# Revit family: Hager-GOLF-Flush_mounted-IP40-With_Cover-With_DIN-Hosted-CH-de
name_source: partatom
category: Electrical Equipment
units: mm (PartAtom-declared; Revit-internal decimal feet)

## family parameters
Cut with Voids When Loaded = No
Host = Face
Maintain Annotation Orientation = Yes
Panel Configuration = Two Columns, Circuits Across
Part Type = Panelboard
Room Calculation Point = No
Round Connector Dimension = Use Diameter
Shared = No

## types (20) — shared parameters
BC_MODEL_ID = 1539115
BC_OBJECT_ID = 512264
BC_OBJECT_VERSION = #40
Code hager = ADD-EC000214_EU
EF000003 - Montageart = Unterputz
EF000007 - Farbe = weiss
EF000024 - UV-beständig = No
EF000049 - Tiefe = 97 mm  [stored 0.318241 ft]
EF000116 - RAL-Nummer = 9010
EF000118 - Mit Montageplatte = No
EF000218 - Einbautiefe = 72 mm  [stored 0.23622 ft]
EF001062 - EMV-Ausführung = No
EF001088 - Anbaumöglichkeit = Yes
EF001134 - DIN-Schiene = Yes
EF004462 - Art der Schliessung = sonstige
EF005474 - Schutzart (IP) = IP40
EF006306 - Mit Schloss = No
EF009212 - Ausführung Deckel = geschlossen
EF015941 - Signaldurchlassende Tür = Yes
ETIM class code = EC000214
ETIM class name = Small distribution board
HG000001-Anzahl der Spalten = 1
HG000002-Mit tür = Yes
HG000003-Bereich = GOLF
HG000005-Dicke = 2 mm  [stored 0.00656168 ft]
HG000006-Unterputz = Yes
HG000009-Doppelflügeligen Tür = No
HG000010-Asymmetrische Türen = No
HG000011-Leere Reihen von unten = No
HG000012-Türschwenkwinkel = 90.00°
HG000013-Tür links = No
HG000014-Tür rechts = Yes
HG000015-Sichtbarkeit der Türöffnung = Yes
HG000016-3D-Türsichtbarkeit = Yes
HG000017-Distanz zwischen den Polen = 18 mm  [stored 0.0590551 ft]
HG000060-RAL-number = 9010
HG000099-Onfly Template ID-de-CH = 507532
Manufacturer = Hager
Name = Hager-GOLF-Flush_mounted-IP40-With_Cover-With_DIN-NoHosted-CH-de
Name BIM&CO = Electricity
Name hager = ADD_Enclosures_EC000214
Uniformat = Low Tension Service & Dist.
Uniformat code = D501001
zero-valued in all types: Default Elevation, EF001131 - Innentiefe, HG000007-Anzahl der leeren Spalten, HG000008-Anzahl der leeren Reihen

## per-type parameters (varying)
| type | BC_VARIANT_ID | EF000008 - Breite | EF000040 - Höhe | EF000266 - Anzahl der Reihen | EF000332 - Einbauhöhe | EF000846 - Einbaubreite | EF002950 - Anzahl Teilungseinheiten | EF006244 - Transparenter Deckel/Tür | EF015776 - Erdungsklemmenblock | EF015777 - Neutralleiterklemmenblock | HG000004-Herstellerreferenz | HGEF000266-Anzahl der Reihen | HGEF0002950-Breite in Teilungseinheiten |
| GOLF-Flush_mounted_W204_H225_D97_4_Modular_Spacing-VF104PS | 1169077 | 204 mm | 225 mm  [stored 0.738189 ft] | 1 | 189 mm  [stored 0.620079 ft] | 170 mm  [stored 0.557743 ft] | 4 | No | No | No | VF104PS | 1 | 4 |
| GOLF-Flush_mounted_W204_H225_D97_4_Modular_Spacing-VF104TS | 1169078 | 204 mm | 225 mm  [stored 0.738189 ft] | 1 | 189 mm  [stored 0.620079 ft] | 170 mm  [stored 0.557743 ft] | 4 | Yes | No | No | VF104TS | 1 | 4 |
| GOLF-Flush_mounted_W275_H225_D97_8_Modular_Spacing-VF108PS | 1169079 | 275 mm | 225 mm  [stored 0.738189 ft] | 1 | 189 mm  [stored 0.620079 ft] | 242 mm  [stored 0.793963 ft] | 8 | No | No | No | VF108PS | 1 | 8 |
| GOLF-Flush_mounted_W275_H225_D97_8_Modular_Spacing-VF108TS | 1169080 | 275 mm | 225 mm  [stored 0.738189 ft] | 1 | 189 mm  [stored 0.620079 ft] | 242 mm  [stored 0.793963 ft] | 8 | Yes | No | No | VF108TS | 1 | 8 |
| GOLF-Flush_mounted_W352_H293_D97_12_Modular_Spacing-VF112PS | 1169081 | 352 mm  [stored 1.15486 ft] | 293 mm | 1 | 257 mm  [stored 0.843176 ft] | 318 mm  [stored 1.04331 ft] | 12 | No | Yes | Yes | VF112PS | 1 | 12 |
| GOLF-Flush_mounted_W352_H293_D97_12_Modular_Spacing-VF112TS | 1169082 | 352 mm  [stored 1.15486 ft] | 293 mm | 1 | 257 mm  [stored 0.843176 ft] | 318 mm  [stored 1.04331 ft] | 12 | Yes | Yes | Yes | VF112TS | 1 | 12 |
| GOLF-Flush_mounted_W460_H293_D97_18_Modular_Spacing-VF118PS | 1169083 | 460 mm  [stored 1.50919 ft] | 293 mm | 1 | 257 mm  [stored 0.843176 ft] | 426 mm  [stored 1.39764 ft] | 18 | No | Yes | Yes | VF118PS | 1 | 18 |
| GOLF-Flush_mounted_W460_H293_D97_18_Modular_Spacing-VF118TS | 1169084 | 460 mm  [stored 1.50919 ft] | 293 mm | 1 | 257 mm  [stored 0.843176 ft] | 426 mm  [stored 1.39764 ft] | 18 | Yes | Yes | Yes | VF118TS | 1 | 18 |
| GOLF-Flush_mounted_W532_H293_D97_22_Modular_Spacing-VF122PS | 1169085 | 532 mm  [stored 1.74541 ft] | 293 mm | 1 | 257 mm  [stored 0.843176 ft] | 498 mm  [stored 1.63386 ft] | 22 | No | Yes | Yes | VF122PS | 1 | 22 |
| GOLF-Flush_mounted_W532_H293_D97_22_Modular_Spacing-VF122TS | 1169086 | 532 mm  [stored 1.74541 ft] | 293 mm | 1 | 257 mm  [stored 0.843176 ft] | 498 mm  [stored 1.63386 ft] | 22 | Yes | Yes | Yes | VF122TS | 1 | 22 |
| GOLF-Flush_mounted_W382_H418_D97_12_Modular_Spacing-VF212PS | 1169087 | 382 mm  [stored 1.25328 ft] | 418 mm  [stored 1.37139 ft] | 2 | 382 mm  [stored 1.25328 ft] | 318 mm  [stored 1.04331 ft] | 12 | No | Yes | Yes | VF212PS | 2 | 12 |
| GOLF-Flush_mounted_W382_H418_D97_12_Modular_Spacing-VF212TS | 1169088 | 382 mm  [stored 1.25328 ft] | 418 mm  [stored 1.37139 ft] | 2 | 382 mm  [stored 1.25328 ft] | 318 mm  [stored 1.04331 ft] | 12 | Yes | Yes | Yes | VF212TS | 2 | 12 |
| GOLF-Flush_mounted_W460_H418_D97_18_Modular_Spacing-VF218PS | 1169089 | 460 mm  [stored 1.50919 ft] | 418 mm  [stored 1.37139 ft] | 2 | 382 mm  [stored 1.25328 ft] | 426 mm  [stored 1.39764 ft] | 18 | No | Yes | Yes | VF218PS | 2 | 18 |
| GOLF-Flush_mounted_W460_H418_D97_18_Modular_Spacing-VF218TS | 1169090 | 460 mm  [stored 1.50919 ft] | 418 mm  [stored 1.37139 ft] | 2 | 382 mm  [stored 1.25328 ft] | 426 mm  [stored 1.39764 ft] | 18 | Yes | Yes | Yes | VF218TS | 2 | 18 |
| GOLF-Flush_mounted_W352_H543_D97_12_Modular_Spacing-VF312PS | 1169091 | 352 mm  [stored 1.15486 ft] | 543 mm  [stored 1.7815 ft] | 3 | 507 mm  [stored 1.66339 ft] | 318 mm  [stored 1.04331 ft] | 12 | No | Yes | Yes | VF312PS | 3 | 12 |
| GOLF-Flush_mounted_W352_H543_D97_12_Modular_Spacing-VF312TS | 1169092 | 352 mm  [stored 1.15486 ft] | 543 mm  [stored 1.7815 ft] | 3 | 507 mm  [stored 1.66339 ft] | 318 mm  [stored 1.04331 ft] | 12 | Yes | Yes | Yes | VF312TS | 3 | 12 |
| GOLF-Flush_mounted_W460_H543_D97_18_Modular_Spacing-VF318PS | 1169093 | 460 mm  [stored 1.50919 ft] | 543 mm  [stored 1.7815 ft] | 3 | 507 mm  [stored 1.66339 ft] | 426 mm  [stored 1.39764 ft] | 18 | No | Yes | Yes | VF318PS | 3 | 18 |
| GOLF-Flush_mounted_W460_H543_D97_18_Modular_Spacing-VF318TS | 1169094 | 460 mm  [stored 1.50919 ft] | 543 mm  [stored 1.7815 ft] | 3 | 507 mm  [stored 1.66339 ft] | 426 mm  [stored 1.39764 ft] | 18 | Yes | Yes | Yes | VF318TS | 3 | 18 |
| GOLF-Flush_mounted_W352_H688_D97_12_Modular_Spacing-VF412PS | 1169095 | 352 mm  [stored 1.15486 ft] | 688 mm  [stored 2.25722 ft] | 4 | 652 mm  [stored 2.13911 ft] | 318 mm  [stored 1.04331 ft] | 12 | No | Yes | Yes | VF412PS | 4 | 12 |
| GOLF-Flush_mounted_W460_H688_D97_18_Modular_Spacing-VF418PS | 1169096 | 460 mm  [stored 1.50919 ft] | 688 mm  [stored 2.25722 ft] | 4 | 652 mm  [stored 2.13911 ft] | 426 mm  [stored 1.39764 ft] | 18 | No | Yes | Yes | VF418PS | 4 | 18 |

note: column(s) folded — value = type name in every type: Reference

note: [stored X ft] marks values corroborated as IEEE doubles in the binary element streams (Revit-internal decimal feet)

## geometry (parser evidence)
native form markers: Sweep x14
no freeform markers — native parametric forms only
